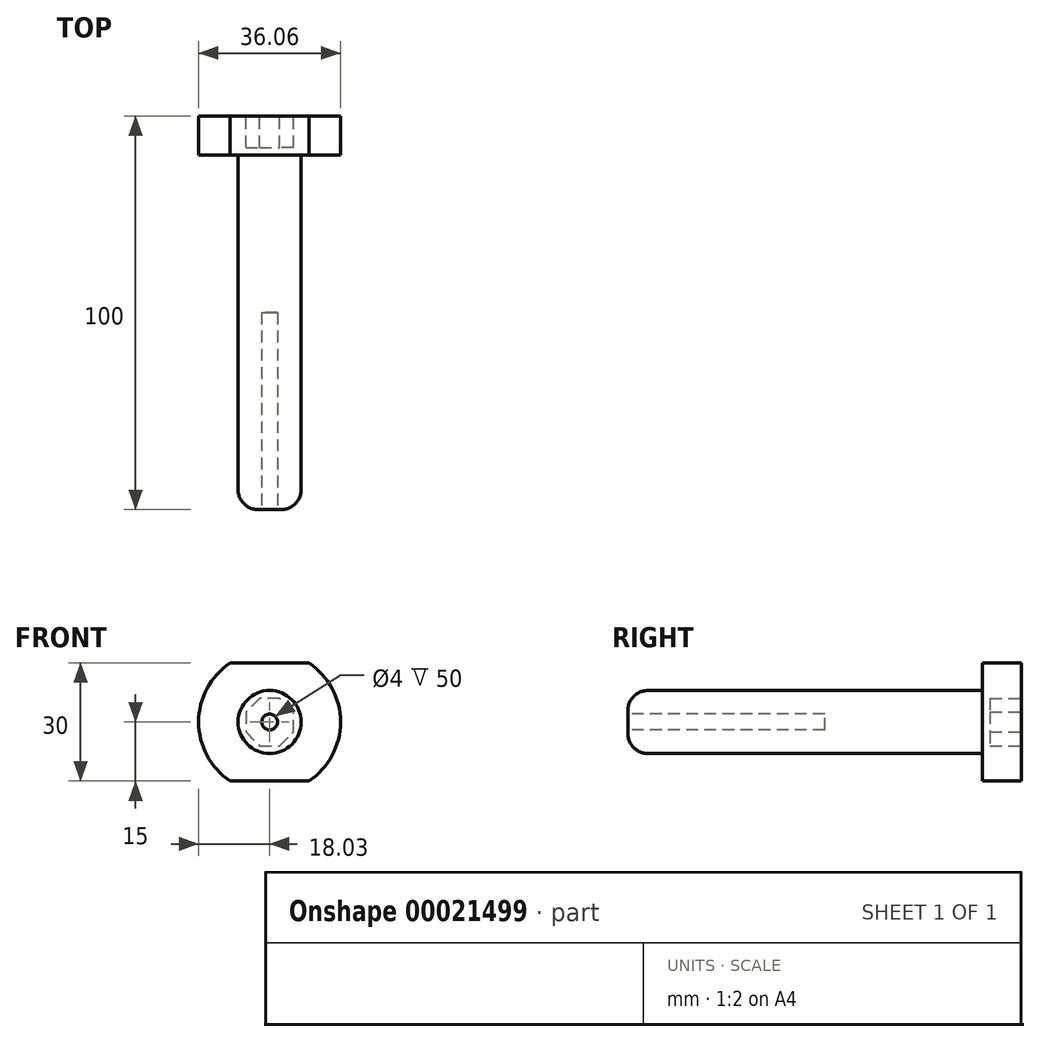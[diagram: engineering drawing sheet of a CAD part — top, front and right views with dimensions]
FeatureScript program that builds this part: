
annotation { "Feature Type Name" : "Feature", "Feature Type Description" : "" }
export const myFeature = defineFeature(function(context is Context, id is Id, definition is map)
    precondition{}
    {
        {
            var Q0;
            Q0=qCreatedBy(makeId("Front.planeOp"),FACE);
            var sketch = newSketch(context, id + "F0", { "sketchPlane" : qUnion([Q0])});
            skCircle(sketch, "E0", {"center": v(0, 0) * mm, "radius": 8 * mm});
            skArc(sketch, "E1", {"start": v(-10, 15) * mm, "mid": v(-18.03, 0) * mm, "end": v(-10, -15) * mm});
            skLineSegment(sketch, "E2.rect.bottom", {"start": v(-10, 15) * mm, "end": v(10, 15) * mm});
            skLineSegment(sketch, "E2.rect.top", {"start": v(-10, -15) * mm, "end": v(10, -15) * mm});
            skArc(sketch, "E3.trimOffspring", {"start": v(10, -15) * mm, "mid": v(18.03, 0) * mm, "end": v(10, 15) * mm});
            skPoint(sketch, "E4.orphan", {"position": v(13.83, -15) * mm});
            skPoint(sketch, "E5.orphan", {"position": v(-13.83, -15) * mm});
            skPoint(sketch, "E6.orphan", {"position": v(-13.83, 15) * mm});
            skPoint(sketch, "E7.orphan", {"position": v(13.83, 15) * mm});
            skSolve(sketch);
        }
        {
            var Q0;
            Q0 = qSketchRegion(id + "F0", true);
            extrude(context, id + "F1", {"entities" : qUnion([Q0]), "depth" : 10 * mm});
        }
        {
            var Q0;
            Q0=makeQuery(id+"F0.imprint","IMPRINT",FACE,{"disambiguationData":[TD([[makeQuery(id+"F0.imprint","IMPRINT",EDGE,{"derivedFrom":sQuery(id+"F0.wireOp",EDGE,"E0")}),1.0]])]});
            extrude(context, id + "F2", {"entities" : qUnion([Q0]), "operationType" : NewBodyOperationType.ADD, "depth" : 100 * mm});
        }
        {
            var Q0;
            Q0=makeQuery(id+"F2.opExtrude","CAP_EDGE",EDGE,{"disambiguationData":[OSD([sQuery(id+"F0.wireOp",EDGE,"E0")])],"isStart":false});
            fillet(context, id + "F3", {"entities" : qUnion([Q0]), "radius" : 5 * mm, "tangentPropagation" : true, "allowEdgeOverflow" : false});
        }
        {
            var Q0;
            Q0=makeQuery(id+"F2.opExtrude","CAP_FACE",FACE,{"disambiguationData":[OSD([sQuery(id+"F0.wireOp",EDGE,"E0")])],"isStart":false});
            var sketch = newSketch(context, id + "F4", { "sketchPlane" : qUnion([Q0])});
            skCircle(sketch, "E8", {"center": v(0, 0) * mm, "radius": 2 * mm});
            skSolve(sketch);
        }
        {
            var Q0;
            Q0=makeQuery(id+"F4.imprint","IMPRINT",FACE,{"disambiguationData":[TD([[makeQuery(id+"F4.imprint","IMPRINT",EDGE,{"derivedFrom":sQuery(id+"F4.wireOp",EDGE,"E8")}),1.0]])]});
            extrude(context, id + "F5", {"entities" : qUnion([Q0]), "operationType" : NewBodyOperationType.REMOVE, "oppositeDirection" : true, "depth" : 50 * mm});
        }
        {
            var Q0;
            {var subQ0=sQuery(id+"F0.wireOp",EDGE,"E0");Q0=makeQuery(id+"F2.boolean.opBoolean","MERGE",FACE,{"derivedFrom":[makeQuery(id+"F1.opExtrude","CAP_FACE",FACE,{"disambiguationData":[OSD([subQ0,sQuery(id+"F0.wireOp",EDGE,"E1"),sQuery(id+"F0.wireOp",EDGE,"E2.rect.bottom"),sQuery(id+"F0.wireOp",EDGE,"E2.rect.top"),sQuery(id+"F0.wireOp",EDGE,"E3.trimOffspring")])],"isStart":true}),makeQuery(id+"F2.opExtrude","CAP_FACE",FACE,{"disambiguationData":[OSD([subQ0])],"isStart":true})]});}
            var sketch = newSketch(context, id + "F6", { "sketchPlane" : qUnion([Q0])});
            skCircle(sketch, "E9.cCircle", {"center": v(0, 0) * mm, "radius": 6.04 * mm, "construction": true});
            skLineSegment(sketch, "E9.0", {"start": v(2.5, -6.04) * mm, "end": v(-2.5, -6.04) * mm});
            skLineSegment(sketch, "E9.1", {"start": v(-2.5, -6.04) * mm, "end": v(-6.04, -2.5) * mm});
            skLineSegment(sketch, "E9.2", {"start": v(-6.04, -2.5) * mm, "end": v(-6.04, 2.5) * mm});
            skLineSegment(sketch, "E9.3", {"start": v(-6.04, 2.5) * mm, "end": v(-2.5, 6.04) * mm});
            skLineSegment(sketch, "E9.4", {"start": v(-2.5, 6.04) * mm, "end": v(2.5, 6.04) * mm});
            skLineSegment(sketch, "E9.5", {"start": v(2.5, 6.04) * mm, "end": v(6.04, 2.5) * mm});
            skLineSegment(sketch, "E9.6", {"start": v(6.04, 2.5) * mm, "end": v(6.04, -2.5) * mm});
            skLineSegment(sketch, "E9.7", {"start": v(6.04, -2.5) * mm, "end": v(2.5, -6.04) * mm});
            skPoint(sketch, "E9.0.midPoint", {"position": v(0, -6.04) * mm});
            skSolve(sketch);
        }
        {
            var Q0;
            Q0 = qSketchRegion(id + "F6", true);
            extrude(context, id + "F7", {"entities" : qUnion([Q0]), "operationType" : NewBodyOperationType.REMOVE, "oppositeDirection" : true, "depth" : 8 * mm});
        }
    });
